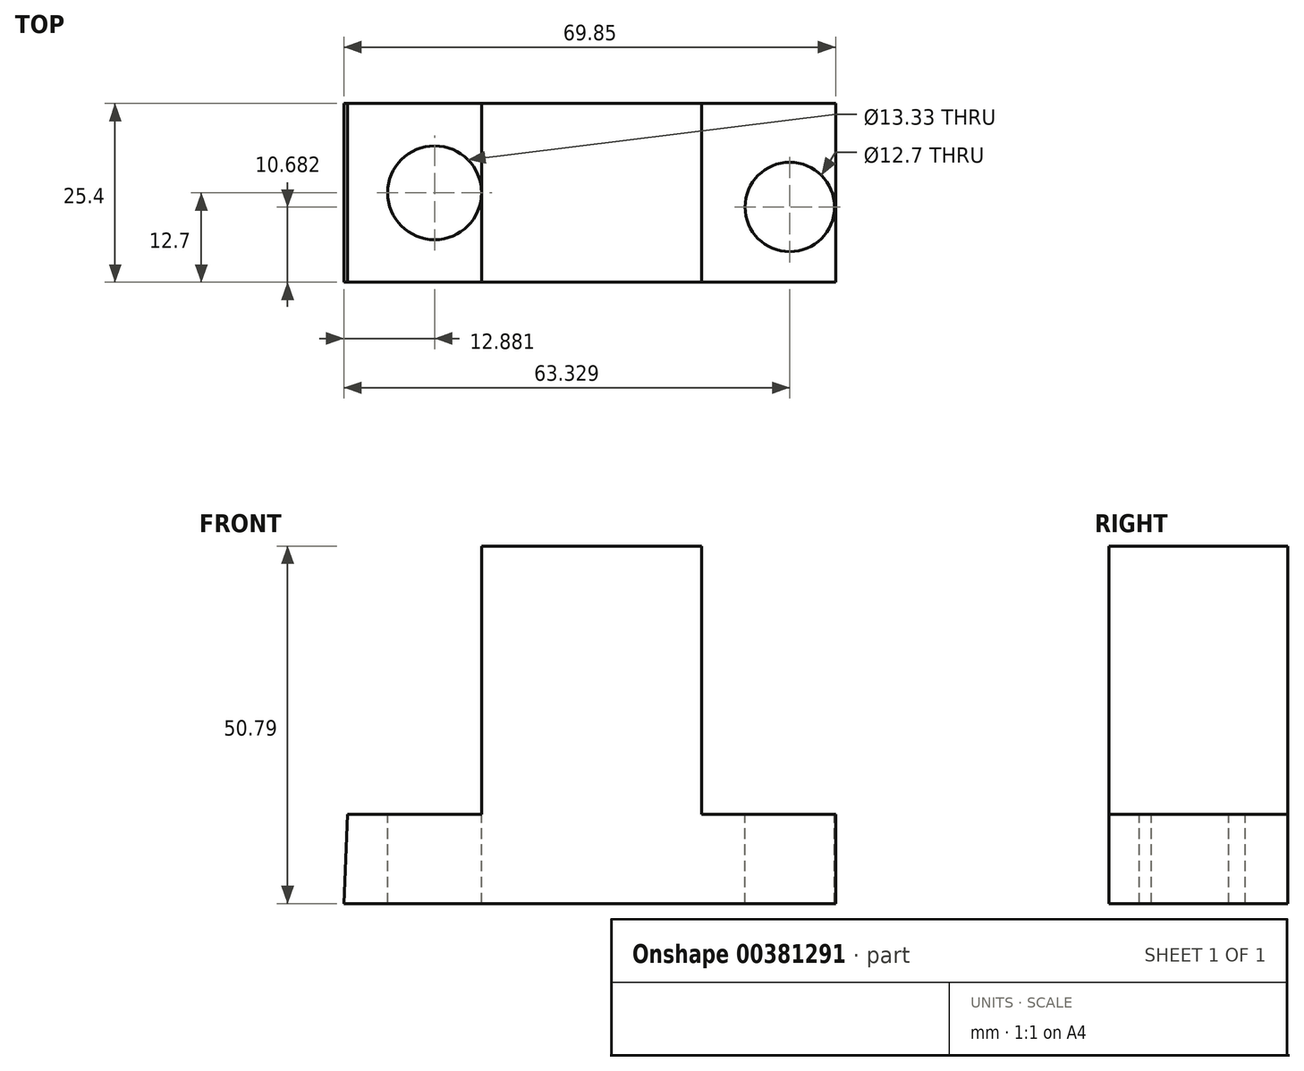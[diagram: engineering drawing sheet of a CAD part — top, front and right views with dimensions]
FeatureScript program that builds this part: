
annotation { "Feature Type Name" : "Feature", "Feature Type Description" : "" }
export const myFeature = defineFeature(function(context is Context, id is Id, definition is map)
    precondition{}
    {
        {
            var Q0;
            Q0=qCreatedBy(makeId("Front.planeOp"),FACE);
            var sketch = newSketch(context, id + "F0", { "sketchPlane" : qUnion([Q0])});
            skLineSegment(sketch, "E0", {"start": v(-37.72, 0) * mm, "end": v(32.13, 0) * mm});
            skLineSegment(sketch, "E1", {"start": v(32.13, 0) * mm, "end": v(32.13, 12.7) * mm});
            skLineSegment(sketch, "E2", {"start": v(32.13, 12.7) * mm, "end": v(13.07, 12.7) * mm});
            skLineSegment(sketch, "E3", {"start": v(13.07, 12.7) * mm, "end": v(13.07, 50.8) * mm});
            skLineSegment(sketch, "E4", {"start": v(13.07, 50.8) * mm, "end": v(-18.17, 50.8) * mm});
            skLineSegment(sketch, "E5", {"start": v(-18.17, 50.8) * mm, "end": v(-18.17, 12.7) * mm});
            skLineSegment(sketch, "E6", {"start": v(-18.17, 12.7) * mm, "end": v(-37.22, 12.7) * mm});
            skLineSegment(sketch, "E7", {"start": v(-37.22, 12.7) * mm, "end": v(-37.72, 0) * mm});
            skSolve(sketch);
        }
        {
            var Q0;
            Q0 = qSketchRegion(id + "F0", true);
            extrude(context, id + "F1", {"entities" : qUnion([Q0]), "depth" : 25.4 * mm});
        }
        {
            var Q0;
            Q0=makeQuery(id+"F1.opExtrude","SWEPT_FACE",FACE,{"disambiguationData":[OSD([sQuery(id+"F0.wireOp",EDGE,"E6")])]});
            var sketch = newSketch(context, id + "F2", { "sketchPlane" : qUnion([Q0])});
            skCircle(sketch, "E8", {"center": v(-24.84, -12.7) * mm, "radius": 6.67 * mm});
            skSolve(sketch);
        }
        {
            var Q0;
            Q0=makeQuery(id+"F2.imprint","IMPRINT",FACE,{"disambiguationData":[TD([[makeQuery(id+"F2.imprint","IMPRINT",EDGE,{"derivedFrom":sQuery(id+"F2.wireOp",EDGE,"E8")}),1.0]])]});
            extrude(context, id + "F3", {"entities" : qUnion([Q0]), "operationType" : NewBodyOperationType.REMOVE, "oppositeDirection" : true, "depth" : 12.7 * mm});
        }
        {
            var Q0;
            Q0=makeQuery(id+"F1.opExtrude","SWEPT_FACE",FACE,{"disambiguationData":[OSD([sQuery(id+"F0.wireOp",EDGE,"E2")])]});
            var sketch = newSketch(context, id + "F4", { "sketchPlane" : qUnion([Q0])});
            skCircle(sketch, "E9", {"center": v(25.6, -14.72) * mm, "radius": 6.35 * mm});
            skSolve(sketch);
        }
        {
            var Q0;
            Q0=makeQuery(id+"F4.imprint","IMPRINT",FACE,{"disambiguationData":[TD([[makeQuery(id+"F4.imprint","IMPRINT",EDGE,{"derivedFrom":sQuery(id+"F4.wireOp",EDGE,"E9")}),1.0]])]});
            extrude(context, id + "F5", {"entities" : qUnion([Q0]), "operationType" : NewBodyOperationType.REMOVE, "oppositeDirection" : true, "depth" : 12.7 * mm});
        }
    });
